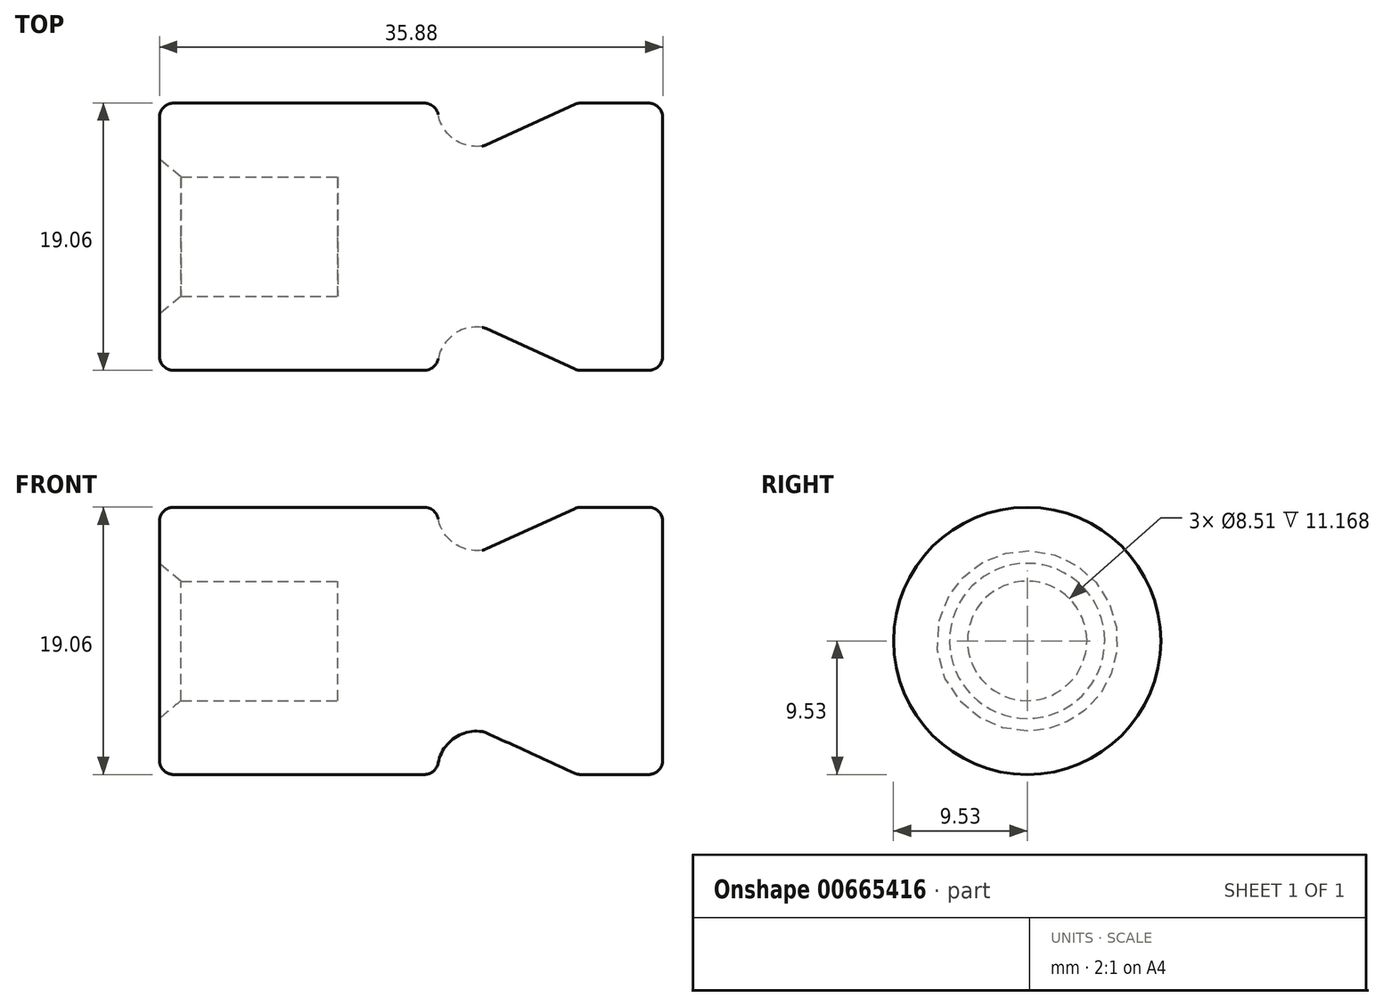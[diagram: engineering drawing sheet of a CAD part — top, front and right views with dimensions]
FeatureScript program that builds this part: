
annotation { "Feature Type Name" : "Feature", "Feature Type Description" : "" }
export const myFeature = defineFeature(function(context is Context, id is Id, definition is map)
    precondition{}
    {
        {
            var Q0;
            Q0=qCreatedBy(makeId("Front.planeOp"),FACE);
            var sketch = newSketch(context, id + "F0", { "sketchPlane" : qUnion([Q0])});
            skLineSegment(sketch, "E0", {"start": v(1.02, 9.53) * mm, "end": v(18.88, 9.53) * mm});
            skLineSegment(sketch, "E1", {"start": v(23.28, 6.55) * mm, "end": v(29.6, 9.43) * mm});
            skLineSegment(sketch, "E2", {"start": v(30.01, 9.52) * mm, "end": v(34.86, 9.52) * mm});
            skLineSegment(sketch, "E3", {"start": v(35.88, 8.5) * mm, "end": v(35.88, 0) * mm});
            skLineSegment(sketch, "E4", {"start": v(35.88, 0) * mm, "end": v(12.71, 0) * mm});
            skArc(sketch, "E5", {"start": v(19.87, 8.7) * mm, "mid": v(20.99, 6.95) * mm, "end": v(23, 6.46) * mm});
            skPoint(sketch, "E6.visualSharp", {"position": v(35.88, 9.53) * mm});
            skArc(sketch, "E6.filletArc", {"start": v(35.88, 8.5) * mm, "mid": v(35.58, 9.23) * mm, "end": v(34.86, 9.53) * mm});
            skPoint(sketch, "E7.visualSharp", {"position": v(29.8, 9.52) * mm});
            skArc(sketch, "E7.filletArc", {"start": v(30.01, 9.53) * mm, "mid": v(29.8, 9.5) * mm, "end": v(29.6, 9.43) * mm});
            skPoint(sketch, "E8.visualSharp", {"position": v(23.16, 6.5) * mm});
            skArc(sketch, "E8.filletArc", {"start": v(23, 6.46) * mm, "mid": v(23.14, 6.5) * mm, "end": v(23.28, 6.55) * mm});
            skPoint(sketch, "E9.visualSharp", {"position": v(19.84, 9.53) * mm});
            skArc(sketch, "E9.filletArc", {"start": v(19.87, 8.7) * mm, "mid": v(19.52, 9.3) * mm, "end": v(18.88, 9.53) * mm});
            skPoint(sketch, "E10.visualSharp", {"position": v(0, 9.53) * mm});
            skArc(sketch, "E10.filletArc", {"start": v(1.02, 9.53) * mm, "mid": v(0.3, 9.23) * mm, "end": v(0, 8.5) * mm});
            skLineSegment(sketch, "E11", {"start": v(1.54, 4.25) * mm, "end": v(12.71, 4.25) * mm});
            skLineSegment(sketch, "E12", {"start": v(12.71, 4.25) * mm, "end": v(12.71, 0) * mm});
            skLineSegment(sketch, "E13", {"start": v(0, 5.53) * mm, "end": v(1.54, 4.25) * mm});
            skLineSegment(sketch, "E14.trimOffspring", {"start": v(0, 5.53) * mm, "end": v(0, 8.5) * mm});
            skSolve(sketch);
        }
        {
            var Q0;
            Q0=makeQuery(id+"F0.imprint","IMPRINT",FACE,{"disambiguationData":[TD([[makeQuery(id+"F0.imprint","IMPRINT",EDGE,{"derivedFrom":sQuery(id+"F0.wireOp",EDGE,"E0")}),-1.0]])]});
            var Q1;
            Q1=sQuery(id+"F0.wireOp",EDGE,"E4");
            revolve(context, id + "F1", {"surfaceOperationType" : NewSurfaceOperationType.NEW, "entities" : qUnion([Q0]), "axis" : qUnion([Q1]), "revolveType" : RevolveType.FULL});
        }
    });
